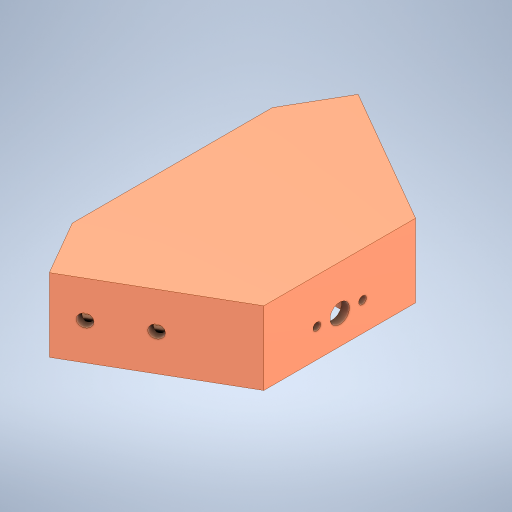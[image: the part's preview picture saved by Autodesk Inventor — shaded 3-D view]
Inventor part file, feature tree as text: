
AUTODESK INVENTOR PART (.ipt)
format: ipt  version: 2024.2 (Build 282272000, 272)  size: 506,880 bytes
history: native  units: mm
features: extrude x11, sketch x11, fillet x1
ambient origin geometry x8: Origin, YZ Plane, XZ Plane, XY Plane, X Axis, Y Axis, Z Axis, Center Point
bodies: Solid1 (feature_tree)
feature tree (23):
  extrude  "Extrusion1"  TaperAngle=150.0deg  [1 undecoded]
  extrude  "Extrusion2"  Depth=20.0mm
  extrude  "Extrusion4"  Depth=4.0mm
  sketch  "Sketch7"  dims[d11=4.0mm d14=28.0mm d15=0.0mm]
  extrude  "Extrusion7"  Depth=28.0mm TaperAngle=0.0deg
  extrude  "Extrusion8"  TaperAngle=0.0deg  [1 undecoded]
  extrude  "Extrusion9"  Depth=5.0mm
  extrude  "Extrusion10"  Depth=10.0mm TaperAngle=0.0deg
  extrude  "Extrusion11"  Depth=60.0mm
  extrude  "Extrusion12"  Depth=40.0mm
  extrude  "Extrusion13"  Depth=7.5mm
  extrude  "Extrusion14"  Depth=1.0mm
  fillet  "Fillet1"  Radius=3.0mm
  sketch  "Sketch1"  dims[d1=60.0deg d3=150.0deg]
  sketch  "Sketch2"  dims[d4=25.0mm d8=20.0mm]
  sketch  "Sketch4"  dims[d9=20.0mm d10=4.0mm]
  sketch  "Sketch8"  dims[d16=4.0mm d17=0.0mm d32=0.0mm d33=0.0mm]
  sketch  "Sketch9"  dims[d48=5.0mm d49=5.0mm]
  sketch  "Sketch10"  dims[d50=10.0mm d51=0.0mm d52=10.0mm d53=0.0mm]
  sketch  "Sketch11"  dims[d54=58.0mm d55=60.0mm]
  sketch  "Sketch12"  dims[d56=40.0mm d57=40.0mm]
  sketch  "Sketch13"  dims[d58=61.0mm d59=7.5mm]
  sketch  "Sketch14"  dims[d60=13.0mm d61=3.0mm d62=3.0mm d63=17.5mm d64=10.0mm d65=0.0mm d66=20.0mm d67=0.0mm d68=20.0mm d69=5.0mm d70=5.0mm d71=10.0mm d72=14.0mm d73=40.0mm d74=0.0mm d75=5.0mm d76=5.0mm d77=20.0mm d78=10.0mm d79=14.5mm d80=40.0mm d81=0.0mm d82=21.0mm d83=21.0mm d84=40.0mm d85=0.0mm d86=21.0mm d87=21.0mm d88=10.5mm d89=2.0mm d90=21.816616mm d91=21.816616mm d92=2.0mm d93=40.0mm d95=360.0deg d97=40.0mm d98=0.0mm d99=2.0mm d100=2.0mm d101=21.816616mm d102=21.816616mm d103=40.0mm d105=360.0deg d107=1.0mm]
note: 2 required parameter values undecoded (feature->parameter linkage not recoverable at this tier; creation-order binding heuristic only, values carry confidence <= 0.55)
